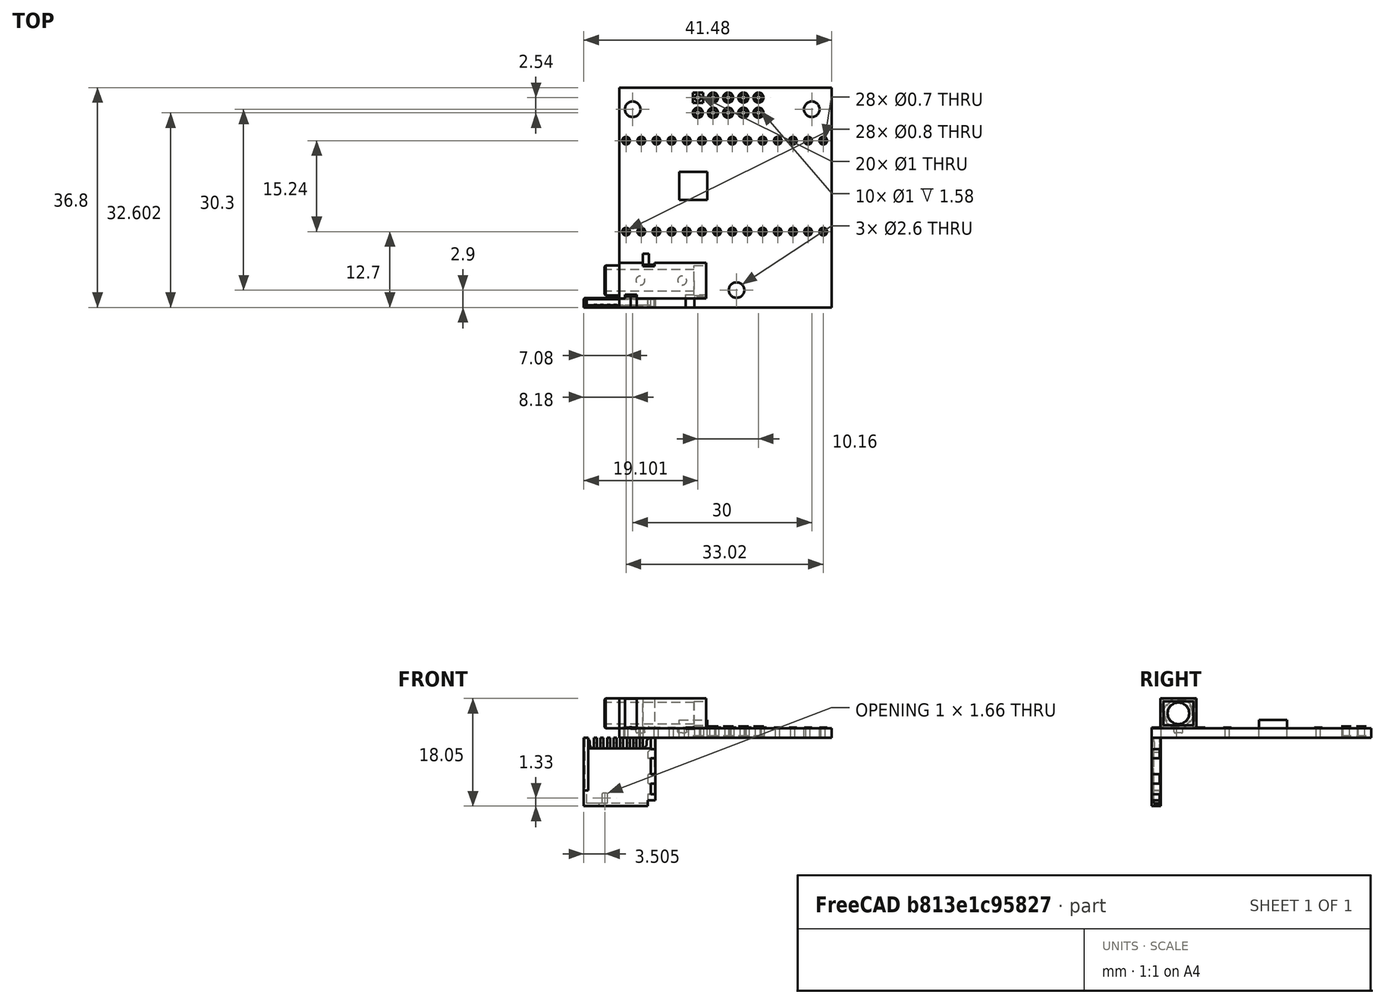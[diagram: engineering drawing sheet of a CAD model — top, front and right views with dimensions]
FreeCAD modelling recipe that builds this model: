
FCSTD DOCUMENT  (FreeCAD 0.18.4R)
Label: TeensyAudioBoard good without extra sdcard
License: All rights reserved
LicenseURL: http://en.wikipedia.org/wiki/All_rights_reserved
objects: Part::Cylinder×19, Part::Cut×19, Part::Feature×11, PartDesign::Body×8, Part::Compound×5, Part::Part2DObjectPython×4, Part::FeaturePython×4, Part::Box×2, App::Part×2, App::DocumentObjectGroup×1
note: 72 computed .brp shape members not serialized (recipe doc carries the construction recipe); baked Part::Feature solids carry a one-line shape summary decoded from their .brp

FEATURE [Part::Feature] Part__Feature  label="CUI_DEVICES_SJ-3523-SMT-TR"
  Placement = pos=(0,4.5,1.6) rot=(1,0,0;1.5708rad)
  shape: bbox 17 x 9 x 5.8 mm, 69 faces (baked)
FEATURE [Part::Box] Box  label="Cube"
  AttacherType = Attacher::AttachEngine3D
  Height = 1.6
  Length = 35.5
  Width = 36.8
FEATURE [Part::Cylinder] Cylinder
  Angle = 360
  AttacherType = Attacher::AttachEngine3D
  Height = 1.6
  Placement = pos=(19.6,2.9,0) rot=(0,0,1;0rad)
  Radius = 1.3
FEATURE [Part::Cut] Cut
  Base = -> Box
  Tool = -> Cylinder
FEATURE [Part::Cylinder] Cylinder001
  Angle = 360
  AttacherType = Attacher::AttachEngine3D
  Height = 1.6
  Placement = pos=(2.2,33.2,0) rot=(0,0,1;0rad)
  Radius = 1.3
FEATURE [Part::Cut] Cut001
  Base = -> Cut
  Tool = -> Cylinder001
FEATURE [Part::Cylinder] Cylinder002
  Angle = 360
  AttacherType = Attacher::AttachEngine3D
  Height = 1.6
  Placement = pos=(32.2,33.2,0) rot=(0,0,1;0rad)
  Radius = 1.3
FEATURE [Part::Cut] Cut002
  Base = -> Cut001
  Tool = -> Cylinder002
FEATURE [Part::Feature] Part__Feature043  label="Component047"
  shape: bbox 0.5 x 0.45 x 1.8 mm, 8 faces (baked)
FEATURE [Part::Feature] Part__Feature044  label="Component048"
  Placement = pos=(4.4,0,9e-15) rot=(0,0,1;0rad)
  shape: bbox 0.5 x 0.45 x 1.8 mm, 8 faces (baked)
FEATURE [Part::Feature] Part__Feature046  label="Component050"
  Placement = pos=(5.5,0,9e-15) rot=(0,0,1;0rad)
  shape: bbox 0.5 x 0.45 x 1.8 mm, 8 faces (baked)
FEATURE [Part::Feature] Part__Feature045  label="Component049"
  Placement = pos=(1.1,0,0) rot=(0,0,1;0rad)
  shape: bbox 0.5 x 0.45 x 1.8 mm, 8 faces (baked)
FEATURE [Part::Feature] Part__Feature047  label="Component051"
  Placement = pos=(6.6,0,0) rot=(0,0,1;0rad)
  shape: bbox 0.5 x 0.45 x 1.8 mm, 8 faces (baked)
FEATURE [Part::Feature] Part__Feature048  label="Component052"
  Placement = pos=(3.3,0,0) rot=(0,0,1;0rad)
  shape: bbox 0.5 x 0.45 x 1.8 mm, 8 faces (baked)
FEATURE [Part::Feature] Part__Feature049  label="Component053"
  Placement = pos=(2.2,0,0) rot=(0,0,1;0rad)
  shape: bbox 0.5 x 0.45 x 1.8 mm, 8 faces (baked)
FEATURE [Part::Feature] Part__Feature050  label="Case"
  shape: bbox 11.95 x 1.55 x 11.45 mm, 59 faces (baked)
FEATURE [App::Part] Pins
  Origin = -> Origin006
FEATURE [Part::Feature] Part__Feature041  label="Base"
  shape: bbox 11.95 x 1.35 x 9.65 mm, 32 faces (baked)
FEATURE [Part::Feature] Part__Feature042  label="Component2"
  Placement = pos=(7.7,0,0) rot=(0,0,1;0rad)
  shape: bbox 0.5 x 0.45 x 1.8 mm, 8 faces (baked)
FEATURE [PartDesign::Body] Body
  Origin = -> Origin
FEATURE [PartDesign::Body] Body001
  Origin = -> Origin008
FEATURE [PartDesign::Body] Body002
  Origin = -> Origin009
FEATURE [PartDesign::Body] Body003
  Origin = -> Origin010
FEATURE [PartDesign::Body] Body004
  Origin = -> Origin011
FEATURE [PartDesign::Body] Body005
  Origin = -> Origin012
FEATURE [PartDesign::Body] Body006
  Origin = -> Origin013
FEATURE [PartDesign::Body] Body007
  Origin = -> Origin014
FEATURE [App::Part] HR5_DM3D_Micro_SD_Card_v4  label="HR5 DM3D Micro SD Card v4"
  Group = -> [Part__Feature041,Pins,Part__Feature050,Body,Body001,Body002,Body003,Body004,Body005,Body006,Body007,Part__Feature042,Part__Feature043,Part__Feature044,Part__Feature045,Part__Feature046,Part__Feature047,Part__Feature048,Part__Feature049]
  Origin = -> Origin007
  Placement = pos=(35.5,20.5,1.6) rot=(0.57735,0.57735,0.57735;2.0944rad)
FEATURE [Part::Cylinder] Cylinder004
  Angle = 360
  AttacherType = Attacher::AttachEngine3D
  Height = 1.6
  Placement = pos=(3.64,12.7,0) rot=(0,0,1;0rad)
  Radius = 0.35
FEATURE [Part::Cylinder] Cylinder008
  Angle = 360
  AttacherType = Attacher::AttachEngine3D
  Height = 1.6
  Placement = pos=(1.1,12.7,0) rot=(0,0,1;0rad)
  Radius = 0.35
FEATURE [Part::Cylinder] Cylinder009
  Angle = 360
  AttacherType = Attacher::AttachEngine3D
  Height = 1.6
  Placement = pos=(8.72,12.7,0) rot=(0,0,1;0rad)
  Radius = 0.35
FEATURE [Part::Cylinder] Cylinder010
  Angle = 360
  AttacherType = Attacher::AttachEngine3D
  Height = 1.6
  Placement = pos=(6.18,12.7,0) rot=(0,0,1;0rad)
  Radius = 0.35
FEATURE [Part::Cylinder] Cylinder011
  Angle = 360
  AttacherType = Attacher::AttachEngine3D
  Height = 1.6
  Placement = pos=(11.26,12.7,0) rot=(0,0,1;0rad)
  Radius = 0.35
FEATURE [Part::Cylinder] Cylinder012
  Angle = 360
  AttacherType = Attacher::AttachEngine3D
  Height = 1.6
  Placement = pos=(13.8,12.7,0) rot=(0,0,1;0rad)
  Radius = 0.35
FEATURE [Part::Cylinder] Cylinder013
  Angle = 360
  AttacherType = Attacher::AttachEngine3D
  Height = 1.6
  Placement = pos=(18.88,12.7,0) rot=(0,0,1;0rad)
  Radius = 0.35
FEATURE [Part::Cylinder] Cylinder014
  Angle = 360
  AttacherType = Attacher::AttachEngine3D
  Height = 1.6
  Placement = pos=(23.96,12.7,0) rot=(0,0,1;0rad)
  Radius = 0.35
FEATURE [Part::Cylinder] Cylinder015
  Angle = 360
  AttacherType = Attacher::AttachEngine3D
  Height = 1.6
  Placement = pos=(21.42,12.7,0) rot=(0,0,1;0rad)
  Radius = 0.35
FEATURE [Part::Cylinder] Cylinder016
  Angle = 360
  AttacherType = Attacher::AttachEngine3D
  Height = 1.6
  Placement = pos=(16.34,12.7,0) rot=(0,0,1;0rad)
  Radius = 0.35
FEATURE [Part::Cylinder] Cylinder017
  Angle = 360
  AttacherType = Attacher::AttachEngine3D
  Height = 1.6
  Placement = pos=(29.04,12.7,0) rot=(0,0,1;0rad)
  Radius = 0.35
FEATURE [Part::Cylinder] Cylinder018
  Angle = 360
  AttacherType = Attacher::AttachEngine3D
  Height = 1.6
  Placement = pos=(34.12,12.7,0) rot=(0,0,1;0rad)
  Radius = 0.35
FEATURE [Part::Cylinder] Cylinder019
  Angle = 360
  AttacherType = Attacher::AttachEngine3D
  Height = 1.6
  Placement = pos=(31.58,12.7,0) rot=(0,0,1;0rad)
  Radius = 0.35
FEATURE [Part::Cylinder] Cylinder020
  Angle = 360
  AttacherType = Attacher::AttachEngine3D
  Height = 1.6
  Placement = pos=(26.5,12.7,0) rot=(0,0,1;0rad)
  Radius = 0.35
FEATURE [Part::Compound] Compound
  Links = -> [Cylinder004,Cylinder008,Cylinder009,Cylinder013,Cylinder018,Cylinder012,Cylinder015,Cylinder014,Cylinder016,Cylinder011,Cylinder010,Cylinder019,Cylinder020,Cylinder017]
FEATURE [Part::Compound] Compound001
  Links = -> [Cylinder004,Cylinder008,Cylinder009,Cylinder013,Cylinder018,Cylinder012,Cylinder015,Cylinder014,Cylinder016,Cylinder011,Cylinder010,Cylinder019,Cylinder020,Cylinder017]
  Placement = pos=(0,15.24,0) rot=(0,0,1;0rad)
FEATURE [Part::Cut] Cut004
  Base = -> Cut002
  Tool = -> Compound
FEATURE [Part::Cut] Cut005
  Base = -> Cut004
  Tool = -> Compound001
FEATURE [Part::Box] Box001  label="Cube001"
  AttacherType = Attacher::AttachEngine3D
  Height = 3
  Length = 4.7
  Placement = pos=(10,18,0) rot=(0,0,1;0rad)
  Width = 4.7
FEATURE [Part::Part2DObjectPython] ShapeString  # Draft 2D object (typed FeaturePython)
  FontFile = <path>
  Placement = pos=(9.41606,9.04423,1.73909) rot=(0,0,1;0rad)
  Size = 2
  String = TEENSY 4 AUDIOBOARD
  Tracking = 0
FEATURE [Part::Part2DObjectPython] Rectangle  # Draft 2D object (typed FeaturePython)
  ChamferSize = 0
  Columns = 1
  FilletRadius = 0
  Height = 5
  Length = 10
  MakeFace = false
  Placement = pos=(-3.86756,8.17618,0.392706) rot=(0,0,1;0rad)
  Rows = 1
FEATURE [Part::Part2DObjectPython] Line  # Draft 2D object (typed FeaturePython)
  ChamferSize = 0
  Closed = false
  End = (0.301227,8.17618,0.392706)
  FilletRadius = 0
  Length = 5
  MakeFace = false
  Placement = pos=(0.301227,13.1762,0.392706) rot=(0,0,1;0rad)
  Points = (2) [(0,0,0),(0,-5,0)]
  Start = (0.301227,13.1762,0.392706)
  Subdivisions = 0
FEATURE [Part::FeaturePython] Connect  label="Connect.[compound]"  # WARN: FeaturePython — macro-defined, semantics opaque (R4)
  Objects = -> [Line,Rectangle]
  Placement = pos=(17.3519,23.21,1.51524) rot=(0,0,1;0rad)
  Tolerance = 0
FEATURE [Part::Cylinder] Cylinder007
  Angle = 360
  AttacherType = Attacher::AttachEngine3D
  Height = 0.1
  Placement = pos=(0,0,1.62) rot=(0,0,1;0rad)
  Radius = 0.4
FEATURE [Part::Cylinder] Cylinder006
  Angle = 360
  AttacherType = Attacher::AttachEngine3D
  Height = 0.1
  Placement = pos=(0,0,1.62) rot=(0,0,1;0rad)
  Radius = 0.65
FEATURE [Part::Cut] Cut003
  Base = -> Cylinder006
  Placement = pos=(1.1,12.7,0) rot=(0,0,1;0rad)
  Tool = -> Cylinder007
FEATURE [Part::Cut] Cut006
  Base = -> Cylinder006
  Placement = pos=(3.64,12.7,0) rot=(0,0,1;0rad)
  Tool = -> Cylinder007
FEATURE [Part::Cut] Cut008
  Base = -> Cylinder006
  Placement = pos=(8.72,12.7,0) rot=(0,0,1;0rad)
  Tool = -> Cylinder007
FEATURE [Part::Cut] Cut009
  Base = -> Cylinder006
  Placement = pos=(11.26,12.7,0) rot=(0,0,1;0rad)
  Tool = -> Cylinder007
FEATURE [Part::Cut] Cut010
  Base = -> Cylinder006
  Placement = pos=(13.8,12.7,0) rot=(0,0,1;0rad)
  Tool = -> Cylinder007
FEATURE [Part::Cut] Cut012
  Base = -> Cylinder006
  Placement = pos=(18.88,12.7,0) rot=(0,0,1;0rad)
  Tool = -> Cylinder007
FEATURE [Part::Cut] Cut013
  Base = -> Cylinder006
  Placement = pos=(21.42,12.7,0) rot=(0,0,1;0rad)
  Tool = -> Cylinder007
FEATURE [Part::Cut] Cut014
  Base = -> Cylinder006
  Placement = pos=(23.96,12.7,0) rot=(0,0,1;0rad)
  Tool = -> Cylinder007
FEATURE [Part::Cut] Cut015
  Base = -> Cylinder006
  Placement = pos=(26.5,12.7,0) rot=(0,0,1;0rad)
  Tool = -> Cylinder007
FEATURE [Part::Cut] Cut016
  Base = -> Cylinder006
  Placement = pos=(29.04,12.7,0) rot=(0,0,1;0rad)
  Tool = -> Cylinder007
FEATURE [Part::Cut] Cut017
  Base = -> Cylinder006
  Placement = pos=(31.58,12.7,0) rot=(0,0,1;0rad)
  Tool = -> Cylinder007
FEATURE [Part::Cut] Cut018
  Base = -> Cylinder006
  Placement = pos=(34.12,12.7,0) rot=(0,0,1;0rad)
  Tool = -> Cylinder007
FEATURE [Part::Cut] Cut011
  Base = -> Cylinder006
  Placement = pos=(16.34,12.7,0) rot=(0,0,1;0rad)
  Tool = -> Cylinder007
FEATURE [Part::Cut] Cut007
  Base = -> Cylinder006
  Placement = pos=(6.18,12.7,0) rot=(0,0,1;0rad)
  Tool = -> Cylinder007
FEATURE [Part::Compound] Compound002
  Links = -> [Cut003,Cut006,Cut018,Cut010,Cut016,Cut013,Cut011,Cut012,Cut017,Cut008,Cut015,Cut009,Cut014,Cut007]
FEATURE [Part::Compound] Compound003
  Links = -> [Cut003,Cut006,Cut018,Cut010,Cut016,Cut013,Cut011,Cut012,Cut017,Cut008,Cut015,Cut009,Cut014,Cut007]
  Placement = pos=(0,15.24,0) rot=(0,0,1;0rad)
FEATURE [Part::Part2DObjectPython] Shape2DView  # Draft 2D object (typed FeaturePython)
  Base = -> Connect
  HiddenLines = false
  InPlace = true
  Projection = (0,0,1)
  ProjectionMode = 0
  SegmentLength = 0.05
  Tessellation = false
  VisibleOnly = false
FEATURE [Part::FeaturePython] TopPads  # a2plus imported part (geometry in sourceFile) (typed FeaturePython)
  Placement = pos=(-2.80293,-6.33255,0) rot=(0,0,1;0rad)
  fixedPosition = true
FEATURE [Part::FeaturePython] BotPads  # a2plus imported part (geometry in sourceFile) (typed FeaturePython)
  Placement = pos=(-2.80293,-6.33255,0) rot=(0,0,1;0rad)
  fixedPosition = true
FEATURE [Part::FeaturePython] THPs  label="PTHs"  # a2plus imported part (geometry in sourceFile) (typed FeaturePython)
  Placement = pos=(-2.80293,-6.33255,0) rot=(0,0,1;0rad)
  fixedPosition = true
FEATURE [App::DocumentObjectGroup] PinSocket_2x05_P2_54mm_Horizontal_fp
  Group = -> [TopPads,BotPads,THPs]
FEATURE [Part::Compound] Compound004
  Links = -> [TopPads,BotPads,THPs]
  Placement = pos=(6.78832,37.945,1.90794) rot=(0,0,1;1.5708rad)
note: 1 file-system path scrubbed to <path> (originals preserved in the JSON sidecar)
